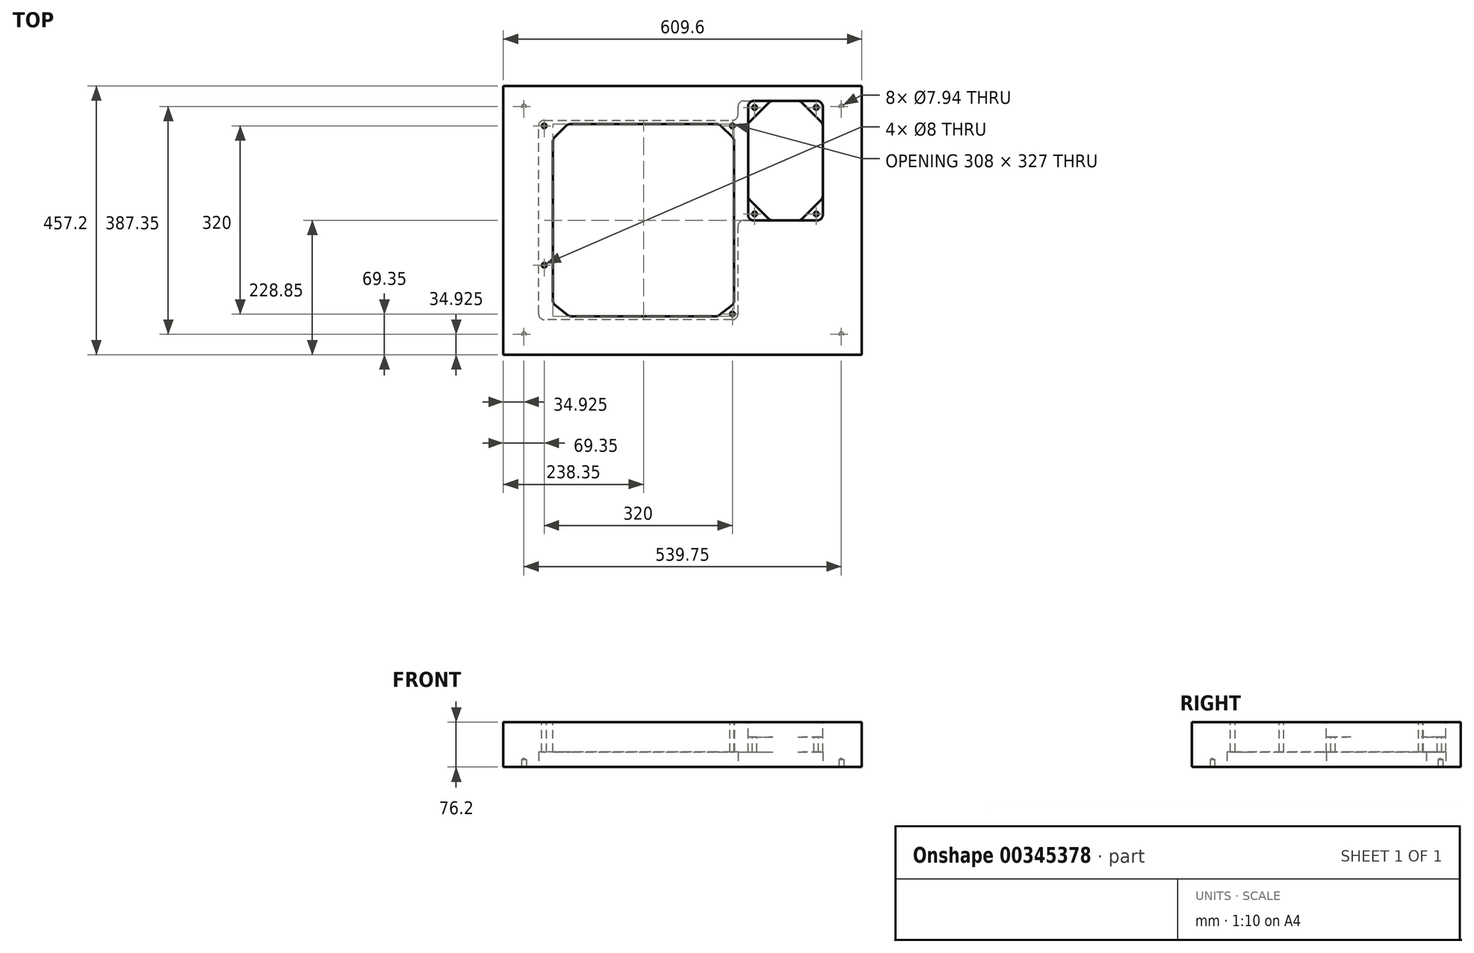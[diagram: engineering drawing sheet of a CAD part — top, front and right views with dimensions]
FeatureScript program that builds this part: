
annotation { "Feature Type Name" : "Feature", "Feature Type Description" : "" }
export const myFeature = defineFeature(function(context is Context, id is Id, definition is map)
    precondition{}
    {
        {
            var Q0;
            Q0=qCreatedBy(makeId("Top.planeOp"),FACE);
            var sketch = newSketch(context, id + "F0", { "sketchPlane" : qUnion([Q0])});
            skLineSegment(sketch, "E0.bottom", {"start": v(0, 0) * mm, "end": v(609.6, 0) * mm});
            skLineSegment(sketch, "E0.top", {"start": v(0, -457.2) * mm, "end": v(609.6, -457.2) * mm});
            skLineSegment(sketch, "E0.left", {"start": v(0, 0) * mm, "end": v(0, -457.2) * mm});
            skLineSegment(sketch, "E0.right", {"start": v(609.6, 0) * mm, "end": v(609.6, -457.2) * mm});
            skSolve(sketch);
        }
        {
            var Q0;
            Q0 = qSketchRegion(id + "F0", true);
            extrude(context, id + "F1", {"entities" : qUnion([Q0]), "oppositeDirection" : true, "depth" : 76.2 * mm});
        }
        {
            var Q0;
            Q0=qCreatedBy(makeId("Top.planeOp"),FACE);
            var sketch = newSketch(context, id + "F2", { "sketchPlane" : qUnion([Q0])});
            skLineSegment(sketch, "E1", {"start": v(367.35, -64.85) * mm, "end": v(109.35, -64.85) * mm});
            skLineSegment(sketch, "E2", {"start": v(109.35, -64.85) * mm, "end": v(84.35, -89.85) * mm});
            skLineSegment(sketch, "E3", {"start": v(84.35, -89.85) * mm, "end": v(84.35, -369.85) * mm});
            skLineSegment(sketch, "E4", {"start": v(84.35, -369.85) * mm, "end": v(112.35, -391.85) * mm});
            skLineSegment(sketch, "E5", {"start": v(112.35, -391.85) * mm, "end": v(364.35, -391.85) * mm});
            skLineSegment(sketch, "E6", {"start": v(364.35, -391.85) * mm, "end": v(392.35, -369.85) * mm});
            skLineSegment(sketch, "E7", {"start": v(392.35, -369.85) * mm, "end": v(392.35, -89.85) * mm});
            skLineSegment(sketch, "E8", {"start": v(392.35, -89.85) * mm, "end": v(367.35, -64.85) * mm});
            skLineSegment(sketch, "E9", {"start": v(240.35, -216.85) * mm, "end": v(240.35, -64.85) * mm, "construction": true});
            skLineSegment(sketch, "E10", {"start": v(240.35, -216.85) * mm, "end": v(392.35, -216.85) * mm, "construction": true});
            skLineSegment(sketch, "E11", {"start": v(240.35, -216.85) * mm, "end": v(84.35, -216.85) * mm, "construction": true});
            skLineSegment(sketch, "E12", {"start": v(240.35, -216.85) * mm, "end": v(240.35, -391.85) * mm, "construction": true});
            skLineSegment(sketch, "E13.bottom", {"start": v(44.35, -44.35) * mm, "end": v(412.85, -44.35) * mm, "construction": true});
            skLineSegment(sketch, "E13.top", {"start": v(44.35, -412.85) * mm, "end": v(412.85, -412.85) * mm, "construction": true});
            skLineSegment(sketch, "E13.left", {"start": v(44.35, -44.35) * mm, "end": v(44.35, -412.85) * mm, "construction": true});
            skLineSegment(sketch, "E13.right", {"start": v(412.85, -44.35) * mm, "end": v(412.85, -412.85) * mm, "construction": true});
            skLineSegment(sketch, "E14", {"start": v(240.35, -64.85) * mm, "end": v(240.35, -44.35) * mm, "construction": true});
            skLineSegment(sketch, "E15", {"start": v(240.35, -391.85) * mm, "end": v(240.35, -412.85) * mm, "construction": true});
            skLineSegment(sketch, "E16", {"start": v(84.35, -216.85) * mm, "end": v(44.35, -216.85) * mm, "construction": true});
            skLineSegment(sketch, "E17", {"start": v(392.35, -216.85) * mm, "end": v(412.85, -216.85) * mm, "construction": true});
            skLineSegment(sketch, "E18", {"start": v(240.35, -44.35) * mm, "end": v(240.35, 0) * mm, "construction": true});
            skLineSegment(sketch, "E19.0", {"start": v(0, 0) * mm, "end": v(609.6, 0) * mm, "construction": true});
            skLineSegment(sketch, "E19.1.0", {"start": v(0, 0) * mm, "end": v(0, -457.2) * mm, "construction": true});
            skLineSegment(sketch, "E19.1.1", {"start": v(0, -457.2) * mm, "end": v(609.6, -457.2) * mm, "construction": true});
            skLineSegment(sketch, "E19.1.2", {"start": v(609.6, -457.2) * mm, "end": v(609.6, 0) * mm, "construction": true});
            skLineSegment(sketch, "E19.1.3", {"start": v(609.6, 0) * mm, "end": v(0, 0) * mm});
            skLineSegment(sketch, "E20", {"start": v(240.35, -412.85) * mm, "end": v(240.35, -457.2) * mm, "construction": true});
            skLineSegment(sketch, "E21", {"start": v(44.35, -216.85) * mm, "end": v(0, -216.85) * mm, "construction": true});
            skSolve(sketch);
        }
        {
            var Q0;
            Q0 = qSketchRegion(id + "F2", true);
            extrude(context, id + "F3", {"entities" : qUnion([Q0]), "operationType" : NewBodyOperationType.REMOVE, "endBound" : BoundingType.THROUGH_ALL, "oppositeDirection" : true, "depth" : 25 * mm});
        }
        {
            var Q0;
            Q0=qCreatedBy(makeId("Top.planeOp"),FACE);
            var sketch = newSketch(context, id + "F4", { "sketchPlane" : qUnion([Q0])});
            skLineSegment(sketch, "E22.0", {"start": v(367.35, -64.85) * mm, "end": v(109.35, -64.85) * mm, "construction": true});
            skLineSegment(sketch, "E22.1", {"start": v(109.35, -64.85) * mm, "end": v(84.35, -89.85) * mm, "construction": true});
            skLineSegment(sketch, "E22.2", {"start": v(84.35, -89.85) * mm, "end": v(84.35, -369.85) * mm, "construction": true});
            skLineSegment(sketch, "E22.3", {"start": v(84.35, -369.85) * mm, "end": v(112.35, -391.85) * mm, "construction": true});
            skLineSegment(sketch, "E22.4", {"start": v(112.35, -391.85) * mm, "end": v(364.35, -391.85) * mm, "construction": true});
            skLineSegment(sketch, "E22.5", {"start": v(364.35, -391.85) * mm, "end": v(392.35, -369.85) * mm, "construction": true});
            skLineSegment(sketch, "E22.6", {"start": v(392.35, -369.85) * mm, "end": v(392.35, -89.85) * mm, "construction": true});
            skLineSegment(sketch, "E22.7", {"start": v(392.35, -89.85) * mm, "end": v(367.35, -64.85) * mm, "construction": true});
            skLineSegment(sketch, "E22.8", {"start": v(240.35, -216.85) * mm, "end": v(240.35, -64.85) * mm, "construction": true});
            skLineSegment(sketch, "E22.9", {"start": v(240.35, -216.85) * mm, "end": v(392.35, -216.85) * mm, "construction": true});
            skLineSegment(sketch, "E22.10", {"start": v(240.35, -216.85) * mm, "end": v(84.35, -216.85) * mm, "construction": true});
            skLineSegment(sketch, "E22.11", {"start": v(240.35, -216.85) * mm, "end": v(240.35, -391.85) * mm, "construction": true});
            skPoint(sketch, "E23", {"position": v(69.35, -67.85) * mm});
            skPoint(sketch, "E24", {"position": v(389.35, -67.85) * mm});
            skPoint(sketch, "E25", {"position": v(389.35, -387.85) * mm});
            skPoint(sketch, "E26", {"position": v(69.35, -304.85) * mm});
            skLineSegment(sketch, "E27", {"start": v(69.35, -67.85) * mm, "end": v(389.35, -67.85) * mm, "construction": true});
            skLineSegment(sketch, "E28", {"start": v(389.35, -67.85) * mm, "end": v(389.35, -387.85) * mm, "construction": true});
            skLineSegment(sketch, "E29", {"start": v(69.35, -67.85) * mm, "end": v(69.35, -387.85) * mm, "construction": true});
            skLineSegment(sketch, "E30", {"start": v(69.35, -387.85) * mm, "end": v(389.35, -387.85) * mm, "construction": true});
            skSolve(sketch);
        }
        {
            var Q0;
            Q0=sQuery(id+"F4.wireOp",VERTEX,"E23");
            var Q1;
            Q1=sQuery(id+"F4.wireOp",VERTEX,"E24");
            var Q2;
            Q2=sQuery(id+"F4.wireOp",VERTEX,"E25");
            var Q3;
            Q3=sQuery(id+"F4.wireOp",VERTEX,"E26");
            var Q4;
            Q4=makeQuery(id+"F1.opExtrude","SWEPT_BODY",BODY,{"disambiguationData":[OSD([sQuery(id+"F0.wireOp",EDGE,"E0.bottom"),sQuery(id+"F0.wireOp",EDGE,"E0.top"),sQuery(id+"F0.wireOp",EDGE,"E0.left"),sQuery(id+"F0.wireOp",EDGE,"E0.right")])]});
            hole(context, id + "F5", {"style" : HoleStyle.SIMPLE, "endStyle" : HoleEndStyle.THROUGH, "holeDiameter" : 8 * mm, "isTappedThrough" : true, "tappedDepth" : 12 * mm, "tapClearance" : 3, "locations" : qUnion([Q0, Q1, Q2, Q3]), "scope" : qUnion([Q4])});
        }
        {
            var Q0;
            Q0=qCreatedBy(makeId("Top.planeOp"),FACE);
            var sketch = newSketch(context, id + "F6", { "sketchPlane" : qUnion([Q0])});
            skLineSegment(sketch, "E31.bottom", {"start": v(416.03, -25.4) * mm, "end": v(543.03, -25.4) * mm});
            skLineSegment(sketch, "E31.top", {"start": v(416.03, -228.6) * mm, "end": v(543.03, -228.6) * mm});
            skLineSegment(sketch, "E31.left", {"start": v(416.03, -25.4) * mm, "end": v(416.03, -228.6) * mm});
            skLineSegment(sketch, "E31.right", {"start": v(543.03, -25.4) * mm, "end": v(543.03, -228.6) * mm});
            skLineSegment(sketch, "E32.8", {"start": v(240.35, -216.85) * mm, "end": v(240.35, -64.85) * mm, "construction": true});
            skLineSegment(sketch, "E32.9", {"start": v(240.35, -216.85) * mm, "end": v(392.35, -216.85) * mm, "construction": true});
            skLineSegment(sketch, "E32.10", {"start": v(240.35, -216.85) * mm, "end": v(84.35, -216.85) * mm, "construction": true});
            skLineSegment(sketch, "E32.11", {"start": v(240.35, -216.85) * mm, "end": v(240.35, -391.85) * mm, "construction": true});
            skLineSegment(sketch, "E32.12", {"start": v(44.35, -44.35) * mm, "end": v(412.85, -44.35) * mm, "construction": true});
            skLineSegment(sketch, "E32.13", {"start": v(44.35, -412.85) * mm, "end": v(412.85, -412.85) * mm, "construction": true});
            skLineSegment(sketch, "E32.14", {"start": v(44.35, -44.35) * mm, "end": v(44.35, -412.85) * mm, "construction": true});
            skLineSegment(sketch, "E32.15", {"start": v(412.85, -44.35) * mm, "end": v(412.85, -412.85) * mm, "construction": true});
            skLineSegment(sketch, "E32.16", {"start": v(240.35, -64.85) * mm, "end": v(240.35, -44.35) * mm, "construction": true});
            skLineSegment(sketch, "E32.17", {"start": v(240.35, -391.85) * mm, "end": v(240.35, -412.85) * mm, "construction": true});
            skLineSegment(sketch, "E32.18", {"start": v(84.35, -216.85) * mm, "end": v(44.35, -216.85) * mm, "construction": true});
            skLineSegment(sketch, "E32.19", {"start": v(392.35, -216.85) * mm, "end": v(412.85, -216.85) * mm, "construction": true});
            skLineSegment(sketch, "E33", {"start": v(416.03, -228.6) * mm, "end": v(412.85, -228.6) * mm, "construction": true});
            skSolve(sketch);
        }
        {
            var Q0;
            Q0=makeQuery(id+"F6.imprint","IMPRINT",FACE,{"disambiguationData":[TD([[makeQuery(id+"F6.imprint","IMPRINT",EDGE,{"derivedFrom":sQuery(id+"F6.wireOp",EDGE,"E31.bottom")}),-1.0]])]});
            extrude(context, id + "F7", {"entities" : qUnion([Q0]), "operationType" : NewBodyOperationType.REMOVE, "oppositeDirection" : true, "depth" : 25.4 * mm});
        }
        {
            var Q0;
            Q0=qCreatedBy(makeId("Top.planeOp"),FACE);
            var sketch = newSketch(context, id + "F8", { "sketchPlane" : qUnion([Q0])});
            skLineSegment(sketch, "E34.0", {"start": v(416.03, -25.4) * mm, "end": v(543.03, -25.4) * mm, "construction": true});
            skLineSegment(sketch, "E34.1", {"start": v(416.03, -228.6) * mm, "end": v(543.03, -228.6) * mm, "construction": true});
            skLineSegment(sketch, "E34.2", {"start": v(416.03, -25.4) * mm, "end": v(416.03, -228.6) * mm, "construction": true});
            skLineSegment(sketch, "E34.3", {"start": v(543.03, -25.4) * mm, "end": v(543.03, -228.6) * mm, "construction": true});
            skLineSegment(sketch, "E35", {"start": v(416.03, -63.5) * mm, "end": v(454.12, -25.4) * mm});
            skLineSegment(sketch, "E36", {"start": v(454.12, -25.4) * mm, "end": v(504.93, -25.4) * mm});
            skLineSegment(sketch, "E37", {"start": v(504.93, -25.4) * mm, "end": v(543.03, -63.5) * mm});
            skLineSegment(sketch, "E38", {"start": v(543.03, -63.5) * mm, "end": v(543.03, -190.5) * mm});
            skLineSegment(sketch, "E39", {"start": v(543.03, -190.5) * mm, "end": v(504.93, -228.6) * mm});
            skLineSegment(sketch, "E40", {"start": v(504.93, -228.6) * mm, "end": v(454.12, -228.6) * mm});
            skLineSegment(sketch, "E41", {"start": v(454.12, -228.6) * mm, "end": v(416.03, -190.5) * mm});
            skLineSegment(sketch, "E42", {"start": v(416.03, -190.5) * mm, "end": v(416.03, -63.5) * mm});
            skLineSegment(sketch, "E43", {"start": v(454.12, -25.4) * mm, "end": v(454.12, -228.6) * mm, "construction": true});
            skLineSegment(sketch, "E44", {"start": v(504.93, -228.6) * mm, "end": v(504.93, -25.4) * mm, "construction": true});
            skLineSegment(sketch, "E45", {"start": v(543.03, -63.5) * mm, "end": v(416.03, -63.5) * mm, "construction": true});
            skLineSegment(sketch, "E46", {"start": v(416.03, -190.5) * mm, "end": v(543.03, -190.5) * mm, "construction": true});
            skSolve(sketch);
        }
        {
            var Q0;
            Q0 = qSketchRegion(id + "F8", true);
            extrude(context, id + "F9", {"entities" : qUnion([Q0]), "operationType" : NewBodyOperationType.REMOVE, "endBound" : BoundingType.THROUGH_ALL, "oppositeDirection" : true, "depth" : 25.4 * mm});
        }
        {
            var Q0;
            Q0=makeQuery(id+"F1.opExtrude","CAP_FACE",FACE,{"disambiguationData":[OSD([sQuery(id+"F0.wireOp",EDGE,"E0.bottom"),sQuery(id+"F0.wireOp",EDGE,"E0.top"),sQuery(id+"F0.wireOp",EDGE,"E0.left"),sQuery(id+"F0.wireOp",EDGE,"E0.right")])],"isStart":false});
            var sketch = newSketch(context, id + "F10", { "sketchPlane" : qUnion([Q0])});
            skPoint(sketch, "E47.12", {"position": v(69.35, 67.85) * mm});
            skPoint(sketch, "E47.13", {"position": v(389.35, 67.85) * mm});
            skPoint(sketch, "E47.14", {"position": v(389.35, 387.85) * mm});
            skPoint(sketch, "E47.15", {"position": v(69.35, 304.85) * mm});
            skLineSegment(sketch, "E47.16", {"start": v(69.35, 67.85) * mm, "end": v(389.35, 67.85) * mm, "construction": true});
            skLineSegment(sketch, "E47.17", {"start": v(389.35, 67.85) * mm, "end": v(389.35, 387.85) * mm, "construction": true});
            skLineSegment(sketch, "E47.18", {"start": v(69.35, 67.85) * mm, "end": v(69.35, 387.85) * mm, "construction": true});
            skLineSegment(sketch, "E47.19", {"start": v(69.35, 387.85) * mm, "end": v(389.35, 387.85) * mm, "construction": true});
            skLineSegment(sketch, "E48.0", {"start": v(416.03, 25.4) * mm, "end": v(543.03, 25.4) * mm});
            skLineSegment(sketch, "E48.1", {"start": v(416.03, 228.6) * mm, "end": v(543.03, 228.6) * mm});
            skLineSegment(sketch, "E48.3", {"start": v(543.03, 25.4) * mm, "end": v(543.03, 228.6) * mm});
            skLineSegment(sketch, "E49", {"start": v(398.88, 58.33) * mm, "end": v(398.88, 25.4) * mm});
            skLineSegment(sketch, "E50", {"start": v(398.88, 25.4) * mm, "end": v(416.03, 25.4) * mm});
            skLineSegment(sketch, "E51", {"start": v(416.03, 228.6) * mm, "end": v(398.88, 228.6) * mm});
            skLineSegment(sketch, "E52", {"start": v(398.88, 397.38) * mm, "end": v(398.88, 228.6) * mm});
            skLineSegment(sketch, "E53", {"start": v(398.88, 397.38) * mm, "end": v(59.82, 397.38) * mm});
            skLineSegment(sketch, "E54", {"start": v(59.82, 397.38) * mm, "end": v(59.83, 58.33) * mm});
            skLineSegment(sketch, "E55", {"start": v(59.83, 58.33) * mm, "end": v(398.88, 58.33) * mm});
            skLineSegment(sketch, "E56", {"start": v(69.35, 227.85) * mm, "end": v(59.83, 227.85) * mm, "construction": true});
            skLineSegment(sketch, "E57", {"start": v(229.35, 387.85) * mm, "end": v(229.35, 397.38) * mm, "construction": true});
            skLineSegment(sketch, "E58", {"start": v(229.35, 67.85) * mm, "end": v(229.35, 58.33) * mm, "construction": true});
            skLineSegment(sketch, "E59", {"start": v(398.88, 312.99) * mm, "end": v(389.35, 312.99) * mm, "construction": true});
            skSolve(sketch);
        }
        {
            var Q0;
            Q0 = qSketchRegion(id + "F10", true);
            var Q1;
            Q1 = qConstructionFilter(qBodyType(qCreatedBy(id + "F10" ,EDGE), BodyType.WIRE), ConstructionObject.NO);
            extrude(context, id + "F11", {"entities" : qUnion([Q0]), "operationType" : NewBodyOperationType.REMOVE, "surfaceEntities" : qUnion([Q1]), "oppositeDirection" : true, "depth" : 25.4 * mm});
        }
        {
            var Q0;
            Q0=makeQuery(id+"F11.boolean.opBoolean","COPY",EDGE,{"derivedFrom":makeQuery(id+"F11.opExtrude","SWEPT_EDGE",EDGE,{"disambiguationData":[OSD([sQuery(id+"F10.wireOp",EDGE,"077a98f5-ebab-4a6d-98d0-87dbe10ba4b7.0"),sQuery(id+"F10.wireOp",EDGE,"077a98f5-ebab-4a6d-98d0-87dbe10ba4b7.3")])]})});
            var Q1;
            Q1=makeQuery(id+"F11.boolean.opBoolean","COPY",EDGE,{"derivedFrom":makeQuery(id+"F11.opExtrude","SWEPT_EDGE",EDGE,{"disambiguationData":[OSD([sQuery(id+"F10.wireOp",EDGE,"077a98f5-ebab-4a6d-98d0-87dbe10ba4b7.0"),sQuery(id+"F10.wireOp",EDGE,"077a98f5-ebab-4a6d-98d0-87dbe10ba4b7.1")])]})});
            var Q2;
            Q2=makeQuery(id+"F11.boolean.opBoolean","COPY",EDGE,{"derivedFrom":makeQuery(id+"F11.opExtrude","SWEPT_EDGE",EDGE,{"disambiguationData":[OSD([sQuery(id+"F10.wireOp",EDGE,"077a98f5-ebab-4a6d-98d0-87dbe10ba4b7.1"),sQuery(id+"F10.wireOp",EDGE,"077a98f5-ebab-4a6d-98d0-87dbe10ba4b7.2")])]})});
            var Q3;
            Q3=makeQuery(id+"F11.boolean.opBoolean","COPY",EDGE,{"derivedFrom":makeQuery(id+"F11.opExtrude","SWEPT_EDGE",EDGE,{"disambiguationData":[OSD([sQuery(id+"F10.wireOp",EDGE,"077a98f5-ebab-4a6d-98d0-87dbe10ba4b7.2"),sQuery(id+"F10.wireOp",EDGE,"077a98f5-ebab-4a6d-98d0-87dbe10ba4b7.3")])]})});
            var Q4;
            Q4=makeQuery(id+"F3.boolean.opBoolean","COPY",EDGE,{"derivedFrom":makeQuery(id+"F3.opExtrude","SWEPT_EDGE",EDGE,{"disambiguationData":[OSD([sQuery(id+"F2.wireOp",EDGE,"E5"),sQuery(id+"F2.wireOp",EDGE,"E6")])]})});
            var Q5;
            Q5=makeQuery(id+"F3.boolean.opBoolean","COPY",EDGE,{"derivedFrom":makeQuery(id+"F3.opExtrude","SWEPT_EDGE",EDGE,{"disambiguationData":[OSD([sQuery(id+"F2.wireOp",EDGE,"E6"),sQuery(id+"F2.wireOp",EDGE,"E7")])]})});
            var Q6;
            Q6=makeQuery(id+"F3.boolean.opBoolean","COPY",EDGE,{"derivedFrom":makeQuery(id+"F3.opExtrude","SWEPT_EDGE",EDGE,{"disambiguationData":[OSD([sQuery(id+"F2.wireOp",EDGE,"E7"),sQuery(id+"F2.wireOp",EDGE,"E8")])]})});
            var Q7;
            Q7=makeQuery(id+"F3.boolean.opBoolean","COPY",EDGE,{"derivedFrom":makeQuery(id+"F3.opExtrude","SWEPT_EDGE",EDGE,{"disambiguationData":[OSD([sQuery(id+"F2.wireOp",EDGE,"E1"),sQuery(id+"F2.wireOp",EDGE,"E8")])]})});
            var Q8;
            Q8=makeQuery(id+"F3.boolean.opBoolean","COPY",EDGE,{"derivedFrom":makeQuery(id+"F3.opExtrude","SWEPT_EDGE",EDGE,{"disambiguationData":[OSD([sQuery(id+"F2.wireOp",EDGE,"E1"),sQuery(id+"F2.wireOp",EDGE,"E2")])]})});
            var Q9;
            Q9=makeQuery(id+"F3.boolean.opBoolean","COPY",EDGE,{"derivedFrom":makeQuery(id+"F3.opExtrude","SWEPT_EDGE",EDGE,{"disambiguationData":[OSD([sQuery(id+"F2.wireOp",EDGE,"E2"),sQuery(id+"F2.wireOp",EDGE,"E3")])]})});
            var Q10;
            Q10=makeQuery(id+"F3.boolean.opBoolean","COPY",EDGE,{"derivedFrom":makeQuery(id+"F3.opExtrude","SWEPT_EDGE",EDGE,{"disambiguationData":[OSD([sQuery(id+"F2.wireOp",EDGE,"E3"),sQuery(id+"F2.wireOp",EDGE,"E4")])]})});
            var Q11;
            Q11=makeQuery(id+"F3.boolean.opBoolean","COPY",EDGE,{"derivedFrom":makeQuery(id+"F3.opExtrude","SWEPT_EDGE",EDGE,{"disambiguationData":[OSD([sQuery(id+"F2.wireOp",EDGE,"E4"),sQuery(id+"F2.wireOp",EDGE,"E5")])]})});
            var Q12;
            Q12=makeQuery(id+"F11.boolean.opBoolean","COPY",EDGE,{"derivedFrom":makeQuery(id+"F11.opExtrude","SWEPT_EDGE",EDGE,{"disambiguationData":[OSD([sQuery(id+"F10.wireOp",EDGE,"E53"),sQuery(id+"F10.wireOp",EDGE,"E54")])]})});
            var Q13;
            Q13=makeQuery(id+"F11.boolean.opBoolean","COPY",EDGE,{"derivedFrom":makeQuery(id+"F11.opExtrude","SWEPT_EDGE",EDGE,{"disambiguationData":[OSD([sQuery(id+"F10.wireOp",EDGE,"E54"),sQuery(id+"F10.wireOp",EDGE,"E55")])]})});
            var Q14;
            Q14=makeQuery(id+"F11.boolean.opBoolean","COPY",EDGE,{"derivedFrom":makeQuery(id+"F11.opExtrude","SWEPT_EDGE",EDGE,{"disambiguationData":[OSD([sQuery(id+"F10.wireOp",EDGE,"E49"),sQuery(id+"F10.wireOp",EDGE,"E55")])]})});
            var Q15;
            Q15=makeQuery(id+"F11.boolean.opBoolean","COPY",EDGE,{"derivedFrom":makeQuery(id+"F11.opExtrude","SWEPT_EDGE",EDGE,{"disambiguationData":[OSD([sQuery(id+"F10.wireOp",EDGE,"E49"),sQuery(id+"F10.wireOp",EDGE,"E50")])]})});
            var Q16;
            Q16=makeQuery(id+"F11.boolean.opBoolean","COPY",EDGE,{"derivedFrom":makeQuery(id+"F11.opExtrude","SWEPT_EDGE",EDGE,{"disambiguationData":[OSD([sQuery(id+"F10.wireOp",EDGE,"E48.0"),sQuery(id+"F10.wireOp",EDGE,"E48.3")])]})});
            var Q17;
            Q17=makeQuery(id+"F11.boolean.opBoolean","COPY",EDGE,{"derivedFrom":makeQuery(id+"F11.opExtrude","SWEPT_EDGE",EDGE,{"disambiguationData":[OSD([sQuery(id+"F10.wireOp",EDGE,"E48.1"),sQuery(id+"F10.wireOp",EDGE,"E48.3")])]})});
            var Q18;
            Q18=makeQuery(id+"F11.boolean.opBoolean","COPY",EDGE,{"derivedFrom":makeQuery(id+"F11.opExtrude","SWEPT_EDGE",EDGE,{"disambiguationData":[OSD([sQuery(id+"F10.wireOp",EDGE,"E51"),sQuery(id+"F10.wireOp",EDGE,"E52")])]})});
            var Q19;
            Q19=makeQuery(id+"F11.boolean.opBoolean","COPY",EDGE,{"derivedFrom":makeQuery(id+"F11.opExtrude","SWEPT_EDGE",EDGE,{"disambiguationData":[OSD([sQuery(id+"F10.wireOp",EDGE,"E52"),sQuery(id+"F10.wireOp",EDGE,"E53")])]})});
            var Q20;
            Q20=makeQuery(id+"F9.boolean.opBoolean","COPY",EDGE,{"derivedFrom":makeQuery(id+"F9.opExtrude","SWEPT_EDGE",EDGE,{"disambiguationData":[OSD([sQuery(id+"F8.wireOp",EDGE,"E40"),sQuery(id+"F8.wireOp",EDGE,"E41")])]})});
            var Q21;
            Q21=makeQuery(id+"F9.boolean.opBoolean","COPY",EDGE,{"derivedFrom":makeQuery(id+"F9.opExtrude","SWEPT_EDGE",EDGE,{"disambiguationData":[OSD([sQuery(id+"F8.wireOp",EDGE,"E41"),sQuery(id+"F8.wireOp",EDGE,"E42")])]})});
            var Q22;
            Q22=makeQuery(id+"F9.boolean.opBoolean","COPY",EDGE,{"derivedFrom":makeQuery(id+"F9.opExtrude","SWEPT_EDGE",EDGE,{"disambiguationData":[OSD([sQuery(id+"F8.wireOp",EDGE,"E39"),sQuery(id+"F8.wireOp",EDGE,"E40")])]})});
            var Q23;
            Q23=makeQuery(id+"F9.boolean.opBoolean","COPY",EDGE,{"derivedFrom":makeQuery(id+"F9.opExtrude","SWEPT_EDGE",EDGE,{"disambiguationData":[OSD([sQuery(id+"F8.wireOp",EDGE,"E38"),sQuery(id+"F8.wireOp",EDGE,"E39")])]})});
            var Q24;
            Q24=makeQuery(id+"F9.boolean.opBoolean","COPY",EDGE,{"derivedFrom":makeQuery(id+"F9.opExtrude","SWEPT_EDGE",EDGE,{"disambiguationData":[OSD([sQuery(id+"F8.wireOp",EDGE,"E35"),sQuery(id+"F8.wireOp",EDGE,"E42")])]})});
            var Q25;
            Q25=makeQuery(id+"F9.boolean.opBoolean","COPY",EDGE,{"derivedFrom":makeQuery(id+"F9.opExtrude","SWEPT_EDGE",EDGE,{"disambiguationData":[OSD([sQuery(id+"F8.wireOp",EDGE,"E35"),sQuery(id+"F8.wireOp",EDGE,"E36")])]})});
            var Q26;
            Q26=makeQuery(id+"F9.boolean.opBoolean","COPY",EDGE,{"derivedFrom":makeQuery(id+"F9.opExtrude","SWEPT_EDGE",EDGE,{"disambiguationData":[OSD([sQuery(id+"F8.wireOp",EDGE,"E36"),sQuery(id+"F8.wireOp",EDGE,"E37")])]})});
            var Q27;
            Q27=makeQuery(id+"F9.boolean.opBoolean","COPY",EDGE,{"derivedFrom":makeQuery(id+"F9.opExtrude","SWEPT_EDGE",EDGE,{"disambiguationData":[OSD([sQuery(id+"F8.wireOp",EDGE,"E37"),sQuery(id+"F8.wireOp",EDGE,"E38")])]})});
            var Q28;
            Q28=makeQuery(id+"F7.boolean.opBoolean","COPY",EDGE,{"derivedFrom":makeQuery(id+"F7.opExtrude","SWEPT_EDGE",EDGE,{"disambiguationData":[OSD([sQuery(id+"F6.wireOp",EDGE,"E31.bottom"),sQuery(id+"F6.wireOp",EDGE,"E31.left")])]})});
            var Q29;
            Q29=makeQuery(id+"F7.boolean.opBoolean","COPY",EDGE,{"derivedFrom":makeQuery(id+"F7.opExtrude","SWEPT_EDGE",EDGE,{"disambiguationData":[OSD([sQuery(id+"F6.wireOp",EDGE,"E31.bottom"),sQuery(id+"F6.wireOp",EDGE,"E31.right")])]})});
            var Q30;
            Q30=makeQuery(id+"F7.boolean.opBoolean","COPY",EDGE,{"derivedFrom":makeQuery(id+"F7.opExtrude","SWEPT_EDGE",EDGE,{"disambiguationData":[OSD([sQuery(id+"F6.wireOp",EDGE,"E31.top"),sQuery(id+"F6.wireOp",EDGE,"E31.left")])]})});
            var Q31;
            Q31=makeQuery(id+"F7.boolean.opBoolean","COPY",EDGE,{"derivedFrom":makeQuery(id+"F7.opExtrude","SWEPT_EDGE",EDGE,{"disambiguationData":[OSD([sQuery(id+"F6.wireOp",EDGE,"E31.top"),sQuery(id+"F6.wireOp",EDGE,"E31.right")])]})});
            fillet(context, id + "F12", {"entities" : qUnion([Q0, Q1, Q2, Q3, Q4, Q5, Q6, Q7, Q8, Q9, Q10, Q11, Q12, Q13, Q14, Q15, Q16, Q17, Q18, Q19, Q20, Q21, Q22, Q23, Q24, Q25, Q26, Q27, Q28, Q29, Q30, Q31]), "radius" : 9.52 * mm, "tangentPropagation" : true, "allowEdgeOverflow" : false});
        }
        {
            var Q0;
            Q0=qCreatedBy(makeId("Top.planeOp"),FACE);
            var sketch = newSketch(context, id + "F13", { "sketchPlane" : qUnion([Q0])});
            skLineSegment(sketch, "E60.0", {"start": v(416.03, -34.92) * mm, "end": v(416.03, -219.08) * mm, "construction": true});
            skArc(sketch, "E60.1", {"start": v(425.55, -228.6) * mm, "mid": v(418.81, -225.81) * mm, "end": v(416.03, -219.08) * mm, "construction": true});
            skLineSegment(sketch, "E60.2", {"start": v(425.55, -228.6) * mm, "end": v(533.5, -228.6) * mm, "construction": true});
            skArc(sketch, "E60.3", {"start": v(458.07, -228.6) * mm, "mid": v(454.43, -227.87) * mm, "end": v(451.34, -225.81) * mm, "construction": true});
            skLineSegment(sketch, "E60.4", {"start": v(451.34, -225.81) * mm, "end": v(418.81, -193.29) * mm, "construction": true});
            skArc(sketch, "E60.5", {"start": v(418.81, -193.29) * mm, "mid": v(416.75, -190.2) * mm, "end": v(416.03, -186.55) * mm, "construction": true});
            skArc(sketch, "E60.6", {"start": v(543.03, -219.08) * mm, "mid": v(540.24, -225.81) * mm, "end": v(533.5, -228.6) * mm, "construction": true});
            skLineSegment(sketch, "E60.7", {"start": v(543.03, -34.92) * mm, "end": v(543.03, -219.08) * mm, "construction": true});
            skArc(sketch, "E60.8", {"start": v(543.03, -186.55) * mm, "mid": v(542.3, -190.2) * mm, "end": v(540.24, -193.29) * mm, "construction": true});
            skLineSegment(sketch, "E60.9", {"start": v(540.24, -193.29) * mm, "end": v(507.71, -225.81) * mm, "construction": true});
            skArc(sketch, "E60.10", {"start": v(507.71, -225.81) * mm, "mid": v(504.62, -227.87) * mm, "end": v(500.98, -228.6) * mm, "construction": true});
            skArc(sketch, "E60.11", {"start": v(540.24, -60.71) * mm, "mid": v(542.3, -63.8) * mm, "end": v(543.03, -67.45) * mm, "construction": true});
            skLineSegment(sketch, "E60.12", {"start": v(507.71, -28.19) * mm, "end": v(540.24, -60.71) * mm, "construction": true});
            skArc(sketch, "E60.13", {"start": v(500.98, -25.4) * mm, "mid": v(504.62, -26.13) * mm, "end": v(507.71, -28.19) * mm, "construction": true});
            skLineSegment(sketch, "E60.14", {"start": v(425.55, -25.4) * mm, "end": v(533.5, -25.4) * mm, "construction": true});
            skArc(sketch, "E60.15", {"start": v(533.5, -25.4) * mm, "mid": v(540.24, -28.19) * mm, "end": v(543.03, -34.92) * mm, "construction": true});
            skArc(sketch, "E60.16", {"start": v(451.34, -28.19) * mm, "mid": v(454.43, -26.13) * mm, "end": v(458.07, -25.4) * mm, "construction": true});
            skLineSegment(sketch, "E60.17", {"start": v(418.81, -60.71) * mm, "end": v(451.34, -28.19) * mm, "construction": true});
            skArc(sketch, "E60.18", {"start": v(416.03, -67.45) * mm, "mid": v(416.75, -63.8) * mm, "end": v(418.81, -60.71) * mm, "construction": true});
            skArc(sketch, "E60.19", {"start": v(416.03, -34.92) * mm, "mid": v(418.81, -28.19) * mm, "end": v(425.55, -25.4) * mm, "construction": true});
            skLineSegment(sketch, "E61", {"start": v(435.08, -44.45) * mm, "end": v(418.81, -28.19) * mm, "construction": true});
            skLineSegment(sketch, "E62", {"start": v(435.07, -209.55) * mm, "end": v(418.81, -225.81) * mm, "construction": true});
            skLineSegment(sketch, "E63", {"start": v(523.98, -209.55) * mm, "end": v(540.24, -225.81) * mm, "construction": true});
            skLineSegment(sketch, "E64", {"start": v(523.98, -44.45) * mm, "end": v(540.24, -28.19) * mm, "construction": true});
            skLineSegment(sketch, "E65.bottom", {"start": v(427.14, -36.51) * mm, "end": v(531.91, -36.51) * mm, "construction": true});
            skLineSegment(sketch, "E65.top", {"start": v(427.14, -217.49) * mm, "end": v(531.91, -217.49) * mm, "construction": true});
            skLineSegment(sketch, "E65.left", {"start": v(427.14, -36.51) * mm, "end": v(427.14, -217.49) * mm, "construction": true});
            skLineSegment(sketch, "E65.right", {"start": v(531.91, -36.51) * mm, "end": v(531.91, -217.49) * mm, "construction": true});
            skSolve(sketch);
        }
        {
            var Q0;
            Q0=sQuery(id+"F13.wireOp",VERTEX,"E65.left.start");
            var Q1;
            Q1=sQuery(id+"F13.wireOp",VERTEX,"E65.bottom.end");
            var Q2;
            Q2=sQuery(id+"F13.wireOp",VERTEX,"E65.right.end");
            var Q3;
            Q3=sQuery(id+"F13.wireOp",VERTEX,"E65.left.end");
            var Q4;
            Q4=makeQuery(id+"F1.opExtrude","SWEPT_BODY",BODY,{"disambiguationData":[OSD([sQuery(id+"F0.wireOp",EDGE,"E0.bottom"),sQuery(id+"F0.wireOp",EDGE,"E0.top"),sQuery(id+"F0.wireOp",EDGE,"E0.left"),sQuery(id+"F0.wireOp",EDGE,"E0.right")])]});
            hole(context, id + "F14", {"style" : HoleStyle.SIMPLE, "endStyle" : HoleEndStyle.THROUGH, "holeDiameter" : 7.94 * mm, "isTappedThrough" : true, "tappedDepth" : 12.7 * mm, "tapClearance" : 3, "locations" : qUnion([Q0, Q1, Q2, Q3]), "scope" : qUnion([Q4])});
        }
        {
            var Q0;
            Q0=makeQuery(id+"F1.opExtrude","CAP_FACE",FACE,{"disambiguationData":[OSD([sQuery(id+"F0.wireOp",EDGE,"E0.bottom"),sQuery(id+"F0.wireOp",EDGE,"E0.top"),sQuery(id+"F0.wireOp",EDGE,"E0.left"),sQuery(id+"F0.wireOp",EDGE,"E0.right")])],"isStart":false});
            var sketch = newSketch(context, id + "F15", { "sketchPlane" : qUnion([Q0])});
            skCircle(sketch, "E66", {"center": v(34.92, 422.28) * mm, "radius": 31.75 * mm, "construction": true});
            skCircle(sketch, "E67", {"center": v(574.68, 422.28) * mm, "radius": 31.75 * mm, "construction": true});
            skCircle(sketch, "E68", {"center": v(574.68, 34.93) * mm, "radius": 31.75 * mm, "construction": true});
            skCircle(sketch, "E69", {"center": v(34.92, 34.92) * mm, "radius": 31.75 * mm, "construction": true});
            skLineSegment(sketch, "E70.bottom", {"start": v(34.92, 422.28) * mm, "end": v(574.68, 422.28) * mm, "construction": true});
            skLineSegment(sketch, "E70.top", {"start": v(34.92, 34.92) * mm, "end": v(574.68, 34.92) * mm, "construction": true});
            skLineSegment(sketch, "E70.left", {"start": v(34.92, 422.28) * mm, "end": v(34.92, 34.92) * mm, "construction": true});
            skLineSegment(sketch, "E70.right", {"start": v(574.68, 422.28) * mm, "end": v(574.68, 34.93) * mm, "construction": true});
            skLineSegment(sketch, "E71", {"start": v(34.93, 34.92) * mm, "end": v(34.93, 0) * mm, "construction": true});
            skLineSegment(sketch, "E72", {"start": v(34.92, 34.92) * mm, "end": v(0, 34.92) * mm, "construction": true});
            skLineSegment(sketch, "E73", {"start": v(574.68, 422.28) * mm, "end": v(574.68, 457.2) * mm, "construction": true});
            skLineSegment(sketch, "E74", {"start": v(574.68, 422.28) * mm, "end": v(609.6, 422.28) * mm, "construction": true});
            skSolve(sketch);
        }
        {
            var Q0;
            Q0=sQuery(id+"F15.wireOp",VERTEX,"E66.center");
            var Q1;
            Q1=sQuery(id+"F15.wireOp",VERTEX,"E70.right.start");
            var Q2;
            Q2=sQuery(id+"F15.wireOp",VERTEX,"E70.right.end");
            var Q3;
            Q3=sQuery(id+"F15.wireOp",VERTEX,"E72.start");
            var Q4;
            Q4=makeQuery(id+"F1.opExtrude","SWEPT_BODY",BODY,{"disambiguationData":[OSD([sQuery(id+"F0.wireOp",EDGE,"E0.bottom"),sQuery(id+"F0.wireOp",EDGE,"E0.top"),sQuery(id+"F0.wireOp",EDGE,"E0.left"),sQuery(id+"F0.wireOp",EDGE,"E0.right")])]});
            hole(context, id + "F16", {"style" : HoleStyle.SIMPLE, "endStyle" : HoleEndStyle.BLIND, "holeDiameter" : 7.94 * mm, "holeDepth" : 12.7 * mm, "isTappedThrough" : true, "tappedDepth" : 12.7 * mm, "tapClearance" : 3, "locations" : qUnion([Q0, Q1, Q2, Q3]), "scope" : qUnion([Q4])});
        }
    });
